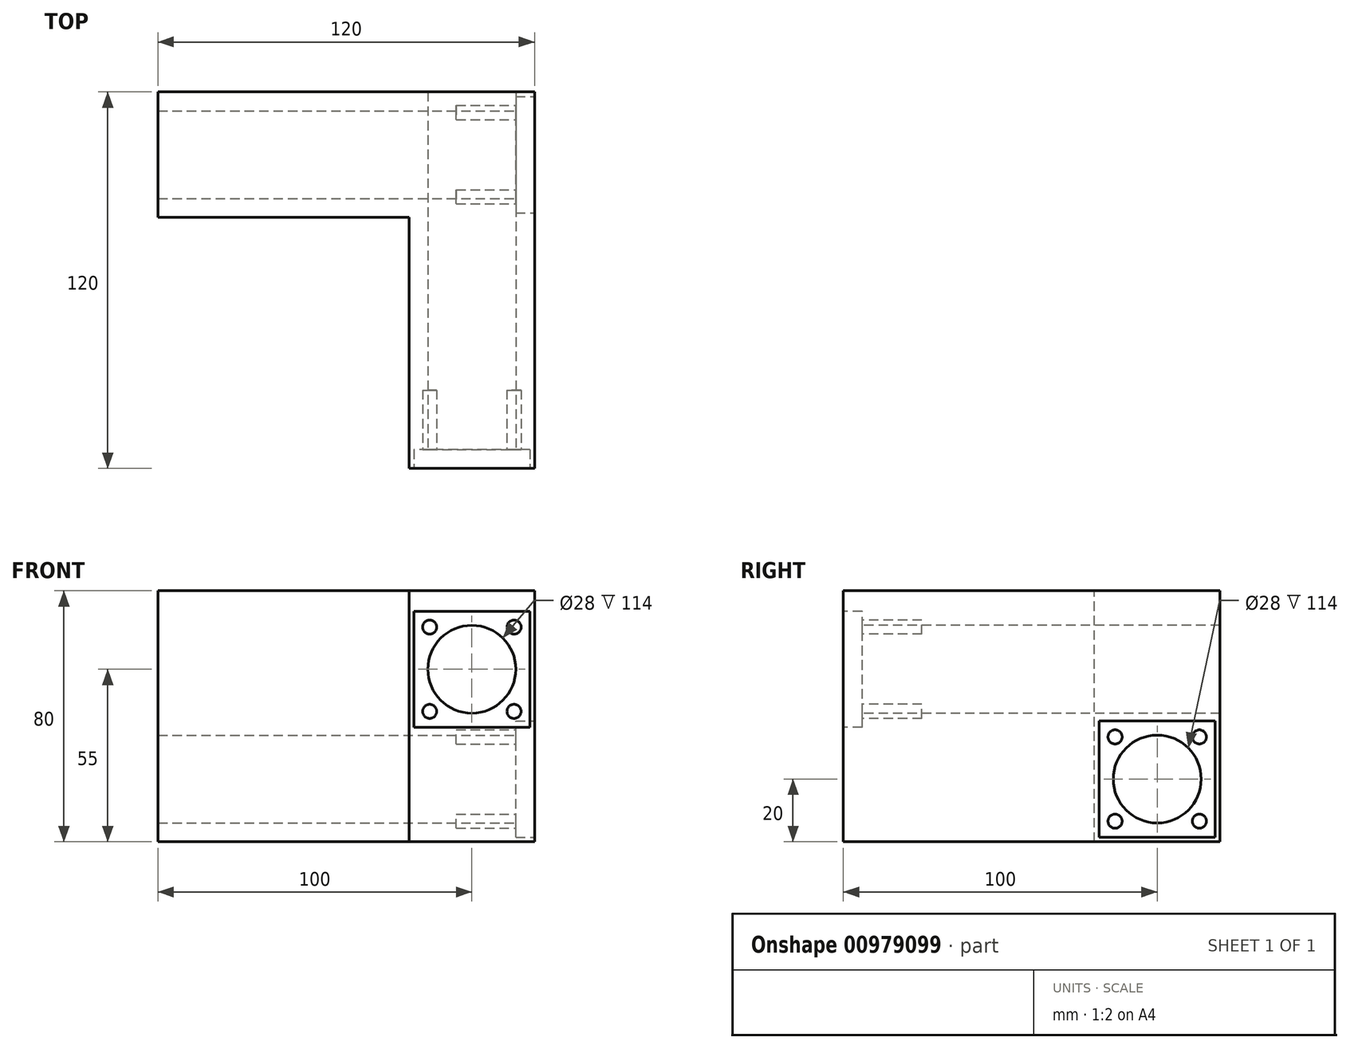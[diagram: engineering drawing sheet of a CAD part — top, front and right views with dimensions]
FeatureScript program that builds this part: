
annotation { "Feature Type Name" : "Feature", "Feature Type Description" : "" }
export const myFeature = defineFeature(function(context is Context, id is Id, definition is map)
    precondition{}
    {
        {
            var Q0;
            Q0=qCreatedBy(makeId("Top.planeOp"),FACE);
            var sketch = newSketch(context, id + "F0", { "sketchPlane" : qUnion([Q0])});
            skLineSegment(sketch, "E0.bottom", {"start": v(60, -60) * mm, "end": v(-60, -60) * mm});
            skLineSegment(sketch, "E0.top", {"start": v(60, 60) * mm, "end": v(-60, 60) * mm});
            skLineSegment(sketch, "E0.left", {"start": v(60, -60) * mm, "end": v(60, 60) * mm});
            skLineSegment(sketch, "E0.right", {"start": v(-60, -60) * mm, "end": v(-60, 60) * mm});
            skPoint(sketch, "E0.middle", {"position": v(0, 0) * mm});
            skSolve(sketch);
        }
        {
            var Q0;
            Q0=qSketchRegion(id+"F0",true);
            extrude(context, id + "F1", {"entities" : qUnion([Q0]), "depth" : 80 * mm, "offsetDistance" : 25 * mm});
        }
        {
            var Q0;
            Q0=makeQuery(id+"F1.opExtrude","SWEPT_FACE",FACE,{"disambiguationData":[OSD([sQuery(id+"F0.wireOp",EDGE,"E0.bottom")])]});
            var sketch = newSketch(context, id + "F2", { "sketchPlane" : qUnion([Q0])});
            skLineSegment(sketch, "E1.bottom", {"start": v(58.5, 36.5) * mm, "end": v(21.5, 36.5) * mm});
            skLineSegment(sketch, "E1.top", {"start": v(58.5, 73.5) * mm, "end": v(21.5, 73.5) * mm});
            skLineSegment(sketch, "E1.left", {"start": v(58.5, 36.5) * mm, "end": v(58.5, 73.5) * mm});
            skLineSegment(sketch, "E1.right", {"start": v(21.5, 36.5) * mm, "end": v(21.5, 73.5) * mm});
            skPoint(sketch, "E1.middle", {"position": v(40, 55) * mm});
            skCircle(sketch, "E2", {"center": v(40, 55) * mm, "radius": 19 * mm, "construction": true});
            skCircle(sketch, "E3", {"center": v(40, 55) * mm, "radius": 14 * mm});
            skLineSegment(sketch, "E4", {"start": v(21.5, 73.5) * mm, "end": v(58.5, 36.5) * mm, "construction": true});
            skLineSegment(sketch, "E5", {"start": v(58.5, 73.5) * mm, "end": v(21.5, 36.5) * mm, "construction": true});
            skPoint(sketch, "E6", {"position": v(26.56, 68.44) * mm});
            skPoint(sketch, "E7", {"position": v(26.56, 41.56) * mm});
            skPoint(sketch, "E8", {"position": v(53.44, 41.56) * mm});
            skPoint(sketch, "E9", {"position": v(53.44, 68.44) * mm});
            skCircle(sketch, "E10", {"center": v(26.56, 68.44) * mm, "radius": 2.25 * mm});
            skCircle(sketch, "E11", {"center": v(53.44, 68.44) * mm, "radius": 2.25 * mm});
            skCircle(sketch, "E12", {"center": v(53.44, 41.56) * mm, "radius": 2.25 * mm});
            skCircle(sketch, "E13", {"center": v(26.56, 41.56) * mm, "radius": 2.25 * mm});
            skSolve(sketch);
        }
        {
            var Q0;
            Q0=qSketchRegion(id+"F2",true);
            var Q1;
            Q1=makeQuery(id+"F2.imprint","IMPRINT",FACE,{"disambiguationData":[TD([[makeQuery(id+"F2.imprint","IMPRINT",EDGE,{"derivedFrom":sQuery(id+"F2.wireOp",EDGE,"E10")}),1.0]])]});
            var Q2;
            Q2=makeQuery(id+"F2.imprint","IMPRINT",FACE,{"disambiguationData":[TD([[makeQuery(id+"F2.imprint","IMPRINT",EDGE,{"derivedFrom":sQuery(id+"F2.wireOp",EDGE,"E3")}),1.0]])]});
            var Q3;
            Q3=makeQuery(id+"F2.imprint","IMPRINT",FACE,{"disambiguationData":[TD([[makeQuery(id+"F2.imprint","IMPRINT",EDGE,{"derivedFrom":sQuery(id+"F2.wireOp",EDGE,"E11")}),1.0]])]});
            var Q4;
            Q4=makeQuery(id+"F2.imprint","IMPRINT",FACE,{"disambiguationData":[TD([[makeQuery(id+"F2.imprint","IMPRINT",EDGE,{"derivedFrom":sQuery(id+"F2.wireOp",EDGE,"E12")}),1.0]])]});
            var Q5;
            Q5=makeQuery(id+"F2.imprint","IMPRINT",FACE,{"disambiguationData":[TD([[makeQuery(id+"F2.imprint","IMPRINT",EDGE,{"derivedFrom":sQuery(id+"F2.wireOp",EDGE,"E13")}),1.0]])]});
            extrude(context, id + "F3", {"entities" : qUnion([Q0, Q1, Q2, Q3, Q4, Q5]), "operationType" : NewBodyOperationType.REMOVE, "oppositeDirection" : true, "depth" : 6 * mm, "offsetDistance" : 25 * mm});
        }
        {
            var Q0;
            Q0=makeQuery(id+"F2.imprint","IMPRINT",FACE,{"disambiguationData":[TD([[makeQuery(id+"F2.imprint","IMPRINT",EDGE,{"derivedFrom":sQuery(id+"F2.wireOp",EDGE,"E3")}),1.0]])]});
            extrude(context, id + "F4", {"entities" : qUnion([Q0]), "operationType" : NewBodyOperationType.REMOVE, "endBound" : BoundingType.THROUGH_ALL, "oppositeDirection" : true, "depth" : 25 * mm, "offsetDistance" : 25 * mm});
        }
        {
            var Q0;
            Q0=makeQuery(id+"F2.imprint","IMPRINT",FACE,{"disambiguationData":[TD([[makeQuery(id+"F2.imprint","IMPRINT",EDGE,{"derivedFrom":sQuery(id+"F2.wireOp",EDGE,"E10")}),1.0]])]});
            var Q1;
            Q1=makeQuery(id+"F2.imprint","IMPRINT",FACE,{"disambiguationData":[TD([[makeQuery(id+"F2.imprint","IMPRINT",EDGE,{"derivedFrom":sQuery(id+"F2.wireOp",EDGE,"E11")}),1.0]])]});
            var Q2;
            Q2=makeQuery(id+"F2.imprint","IMPRINT",FACE,{"disambiguationData":[TD([[makeQuery(id+"F2.imprint","IMPRINT",EDGE,{"derivedFrom":sQuery(id+"F2.wireOp",EDGE,"E12")}),1.0]])]});
            var Q3;
            Q3=makeQuery(id+"F2.imprint","IMPRINT",FACE,{"disambiguationData":[TD([[makeQuery(id+"F2.imprint","IMPRINT",EDGE,{"derivedFrom":sQuery(id+"F2.wireOp",EDGE,"E13")}),1.0]])]});
            extrude(context, id + "F5", {"entities" : qUnion([Q0, Q1, Q2, Q3]), "operationType" : NewBodyOperationType.REMOVE, "oppositeDirection" : true, "depth" : 25 * mm, "offsetDistance" : 25 * mm});
        }
        {
            var Q0;
            Q0=makeQuery(id+"F1.opExtrude","SWEPT_FACE",FACE,{"disambiguationData":[OSD([sQuery(id+"F0.wireOp",EDGE,"E0.left")])]});
            var sketch = newSketch(context, id + "F6", { "sketchPlane" : qUnion([Q0])});
            skLineSegment(sketch, "E14.bottom", {"start": v(58.5, 1.5) * mm, "end": v(21.5, 1.5) * mm});
            skLineSegment(sketch, "E14.top", {"start": v(58.5, 38.5) * mm, "end": v(21.5, 38.5) * mm});
            skLineSegment(sketch, "E14.left", {"start": v(58.5, 1.5) * mm, "end": v(58.5, 38.5) * mm});
            skLineSegment(sketch, "E14.right", {"start": v(21.5, 1.5) * mm, "end": v(21.5, 38.5) * mm});
            skPoint(sketch, "E14.middle", {"position": v(40, 20) * mm});
            skCircle(sketch, "E15", {"center": v(40, 20) * mm, "radius": 19 * mm, "construction": true});
            skCircle(sketch, "E16", {"center": v(40, 20) * mm, "radius": 14 * mm});
            skLineSegment(sketch, "E17", {"start": v(21.5, 38.5) * mm, "end": v(58.5, 1.5) * mm, "construction": true});
            skLineSegment(sketch, "E18", {"start": v(58.5, 38.5) * mm, "end": v(21.5, 1.5) * mm, "construction": true});
            skPoint(sketch, "E19", {"position": v(26.56, 33.44) * mm});
            skPoint(sketch, "E20", {"position": v(26.56, 6.56) * mm});
            skPoint(sketch, "E21", {"position": v(53.44, 6.56) * mm});
            skPoint(sketch, "E22", {"position": v(53.44, 33.44) * mm});
            skCircle(sketch, "E23", {"center": v(26.56, 33.44) * mm, "radius": 2.25 * mm});
            skCircle(sketch, "E24", {"center": v(53.44, 33.44) * mm, "radius": 2.25 * mm});
            skCircle(sketch, "E25", {"center": v(53.44, 6.56) * mm, "radius": 2.25 * mm});
            skCircle(sketch, "E26", {"center": v(26.56, 6.56) * mm, "radius": 2.25 * mm});
            skSolve(sketch);
        }
        {
            var Q0;
            Q0=qSketchRegion(id+"F6",true);
            var Q1;
            Q1=makeQuery(id+"F6.imprint","IMPRINT",FACE,{"disambiguationData":[TD([[makeQuery(id+"F6.imprint","IMPRINT",EDGE,{"derivedFrom":sQuery(id+"F6.wireOp",EDGE,"E16")}),1.0]])]});
            var Q2;
            Q2=makeQuery(id+"F6.imprint","IMPRINT",FACE,{"disambiguationData":[TD([[makeQuery(id+"F6.imprint","IMPRINT",EDGE,{"derivedFrom":sQuery(id+"F6.wireOp",EDGE,"E23")}),1.0]])]});
            var Q3;
            Q3=makeQuery(id+"F6.imprint","IMPRINT",FACE,{"disambiguationData":[TD([[makeQuery(id+"F6.imprint","IMPRINT",EDGE,{"derivedFrom":sQuery(id+"F6.wireOp",EDGE,"E24")}),1.0]])]});
            var Q4;
            Q4=makeQuery(id+"F6.imprint","IMPRINT",FACE,{"disambiguationData":[TD([[makeQuery(id+"F6.imprint","IMPRINT",EDGE,{"derivedFrom":sQuery(id+"F6.wireOp",EDGE,"E25")}),1.0]])]});
            var Q5;
            Q5=makeQuery(id+"F6.imprint","IMPRINT",FACE,{"disambiguationData":[TD([[makeQuery(id+"F6.imprint","IMPRINT",EDGE,{"derivedFrom":sQuery(id+"F6.wireOp",EDGE,"E26")}),1.0]])]});
            extrude(context, id + "F7", {"entities" : qUnion([Q0, Q1, Q2, Q3, Q4, Q5]), "operationType" : NewBodyOperationType.REMOVE, "oppositeDirection" : true, "depth" : 6 * mm, "offsetDistance" : 25 * mm});
        }
        {
            var Q0;
            Q0=makeQuery(id+"F6.imprint","IMPRINT",FACE,{"disambiguationData":[TD([[makeQuery(id+"F6.imprint","IMPRINT",EDGE,{"derivedFrom":sQuery(id+"F6.wireOp",EDGE,"E16")}),1.0]])]});
            extrude(context, id + "F8", {"entities" : qUnion([Q0]), "operationType" : NewBodyOperationType.REMOVE, "endBound" : BoundingType.THROUGH_ALL, "oppositeDirection" : true, "depth" : 25 * mm, "offsetDistance" : 25 * mm});
        }
        {
            var Q0;
            Q0=makeQuery(id+"F6.imprint","IMPRINT",FACE,{"disambiguationData":[TD([[makeQuery(id+"F6.imprint","IMPRINT",EDGE,{"derivedFrom":sQuery(id+"F6.wireOp",EDGE,"E23")}),1.0]])]});
            var Q1;
            Q1=makeQuery(id+"F6.imprint","IMPRINT",FACE,{"disambiguationData":[TD([[makeQuery(id+"F6.imprint","IMPRINT",EDGE,{"derivedFrom":sQuery(id+"F6.wireOp",EDGE,"E24")}),1.0]])]});
            var Q2;
            Q2=makeQuery(id+"F6.imprint","IMPRINT",FACE,{"disambiguationData":[TD([[makeQuery(id+"F6.imprint","IMPRINT",EDGE,{"derivedFrom":sQuery(id+"F6.wireOp",EDGE,"E25")}),1.0]])]});
            var Q3;
            Q3=makeQuery(id+"F6.imprint","IMPRINT",FACE,{"disambiguationData":[TD([[makeQuery(id+"F6.imprint","IMPRINT",EDGE,{"derivedFrom":sQuery(id+"F6.wireOp",EDGE,"E26")}),1.0]])]});
            extrude(context, id + "F9", {"entities" : qUnion([Q0, Q1, Q2, Q3]), "operationType" : NewBodyOperationType.REMOVE, "oppositeDirection" : true, "depth" : 25 * mm, "offsetDistance" : 25 * mm});
        }
        {
            var Q0;
            Q0=makeQuery(id+"F1.opExtrude","CAP_FACE",FACE,{"disambiguationData":[OSD([sQuery(id+"F0.wireOp",EDGE,"E0.bottom"),sQuery(id+"F0.wireOp",EDGE,"E0.top"),sQuery(id+"F0.wireOp",EDGE,"E0.left"),sQuery(id+"F0.wireOp",EDGE,"E0.right")])],"isStart":false});
            var sketch = newSketch(context, id + "F10", { "sketchPlane" : qUnion([Q0])});
            skLineSegment(sketch, "E27", {"start": v(20, -60) * mm, "end": v(20, 20) * mm});
            skLineSegment(sketch, "E28", {"start": v(-60, 20) * mm, "end": v(20, 20) * mm});
            skSolve(sketch);
        }
        {
            var Q0;
            {var subQ0=sQuery(id+"F10.wireOp",EDGE,"E27");Q0=makeQuery(id+"F10.imprint","IMPRINT",FACE,{"disambiguationData":[TD([[makeQuery(id+"F10.imprint","IMPRINT",EDGE,{"derivedFrom":subQ0}),1.0]])]});}
            extrude(context, id + "F11", {"entities" : qUnion([Q0]), "operationType" : NewBodyOperationType.REMOVE, "endBound" : BoundingType.THROUGH_ALL, "oppositeDirection" : true, "depth" : 25 * mm, "offsetDistance" : 25 * mm});
        }
    });
